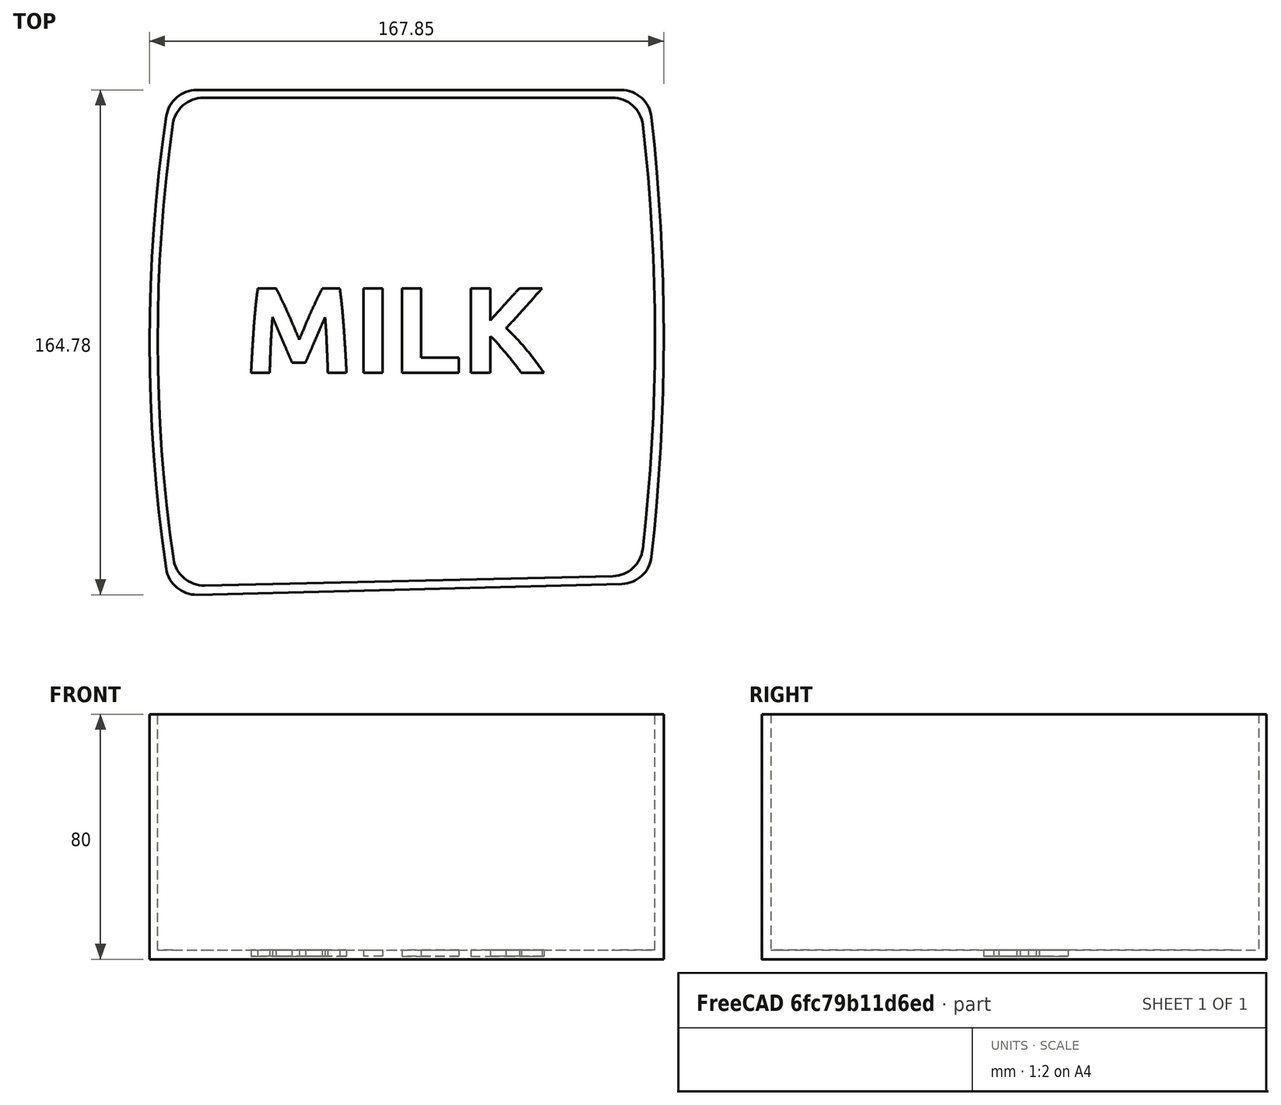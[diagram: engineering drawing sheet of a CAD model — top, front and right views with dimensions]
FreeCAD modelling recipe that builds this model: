
FCSTD DOCUMENT  (FreeCAD 0.19R)
Label: Milk2
License: All rights reserved
LicenseURL: http://en.wikipedia.org/wiki/All_rights_reserved
objects: Sketcher::SketchObject×2, PartDesign::Fillet×2, PartDesign::Pad×1, PartDesign::Pocket×1, PartDesign::Body×1, Part::Part2DObjectPython×1, Part::Extrusion×1, Part::Cut×1, Mesh::Feature×1
note: 14 computed .brp shape members not serialized (recipe doc carries the construction recipe); baked Part::Feature solids carry a one-line shape summary decoded from their .brp

FEATURE [Sketcher::SketchObject] Sketch
  FullyConstrained = false
  MapMode = 5
  Support = -> [XY_Plane]
  sketch-geometry (5):
    g0: ArcOfCircle CenterX=-567.525 CenterY=0 CenterZ=0 NormalX=0 NormalY=0 NormalZ=1 AngleXU=0 Radius=650.525 StartAngle=6.15912 EndAngle=6.40725
    g1: LineSegment StartX=-78 StartY=80.5 StartZ=0 EndX=78 EndY=80.5 EndZ=0
    g2: LineSegment StartX=-78 StartY=-84.5 StartZ=0 EndX=78 EndY=-80.5 EndZ=0
    g3: LineSegment StartX=83 StartY=48.8324 StartZ=0 EndX=83 EndY=-50.184 EndZ=0
    g4: ArcOfCircle CenterX=415.147 CenterY=-2 CenterZ=0 NormalX=0 NormalY=0 NormalZ=1 AngleXU=0 Radius=500 StartAngle=2.97583 EndAngle=3.30735
  constraints (15):
    c: PointOnObject(g0,g-1)
    c: Coincident(g1,g0)
    c: Coincident(g2,g0)
    c: Symmetric(g0,g1,g-2)
    c: Distance(g1) = 156
    c: Vertical(g3)
    c: Tangent(g3,g0)
    c: DistanceX(g0,g3) = 5
    c: DistanceY(g1) = 80.5
    c: DistanceY(g0) = -80.5
    c: DistanceY(g2) = -84.5
    c: DistanceX(g2) = -78
    c: Coincident(g4,g1)
    c: Coincident(g4,g2)
    c: Radius(g4) = 500
FEATURE [PartDesign::Pad] Pad
  Direction = (1,1,1)
  Length = 80
  Length2 = 100
  Profile = -> Sketch
  Type = 0
FEATURE [Sketcher::SketchObject] Sketch001
  FullyConstrained = false
  MapMode = 5
  Placement = pos=(0,0,80) rot=(0,0,1;0rad)
  Support = -> [Pad]
  sketch-geometry (4):
    g0: LineSegment StartX=-75.6334 StartY=-81.4504 StartZ=0 EndX=75.0731 EndY=-78 EndZ=0
    g1: LineSegment StartX=-75.9147 StartY=78 StartZ=0 EndX=75.0731 EndY=78 EndZ=0
    g2: ArcOfCircle CenterX=-519.835 CenterY=0 CenterZ=0 NormalX=0 NormalY=0 NormalZ=1 AngleXU=0 Radius=600 StartAngle=6.15282 EndAngle=6.41355
    g3: ArcOfCircle CenterX=417.828 CenterY=-0.854359 CenterZ=0 NormalX=0 NormalY=0 NormalZ=1 AngleXU=0 Radius=500 StartAngle=2.98322 EndAngle=3.30349
  constraints (11):
    c: PointOnObject(g2,g-1)
    c: Coincident(g2,g1)
    c: Coincident(g2,g0)
    c: DistanceY(g1) = 78
    c: DistanceY(g0) = -78
    c: Radius(g2) = 600
    c: Coincident(g3,g1)
    c: Coincident(g3,g0)
    c: Radius(g3) = 500
    c: DistanceX(g0) = -75.6334
    c: DistanceY(g0) = -81.4504
FEATURE [PartDesign::Pocket] Pocket
  BaseFeature = -> Pad
  Length = 77
  Length2 = 100
  Profile = -> Sketch001
  Type = 0
FEATURE [PartDesign::Fillet] Fillet
  Base = -> Pocket [Edge17,Edge22,Edge18,Edge20]
  BaseFeature = -> Pocket
  Radius = 10
  SupportTransform = false
FEATURE [PartDesign::Fillet] Fillet001
  Base = -> Fillet [Edge30,Edge29,Edge34,Edge32]
  BaseFeature = -> Fillet
  Radius = 10
  SupportTransform = false
FEATURE [PartDesign::Body] Body
  Group = -> [Sketch,Pad,Sketch001,Pocket,Fillet,Fillet001]
  Origin = -> Origin
  Tip = -> Fillet001
FEATURE [Part::Part2DObjectPython] ShapeString001  # Draft 2D object (typed FeaturePython)
  FontFile = <path>
  Placement = pos=(-54.1,-11.85,3) rot=(0,0,1;0rad)
  Size = 15
  String = MILK
  Tracking = 0
FEATURE [Part::Extrusion] Extrude
  Base = -> ShapeString001
  Dir = (0,0,1)
  DirMode = 2
  FaceMakerClass = Part::FaceMakerBullseye
  LengthFwd = -2
  LengthRev = 0
  Solid = false
  Symmetric = false
FEATURE [Part::Cut] Cut
  Base = -> Fillet001
  Tool = -> Extrude
FEATURE [Mesh::Feature] Mesh  label="Cut (Meshed)"
note: 1 file-system path scrubbed to <path> (originals preserved in the JSON sidecar)
